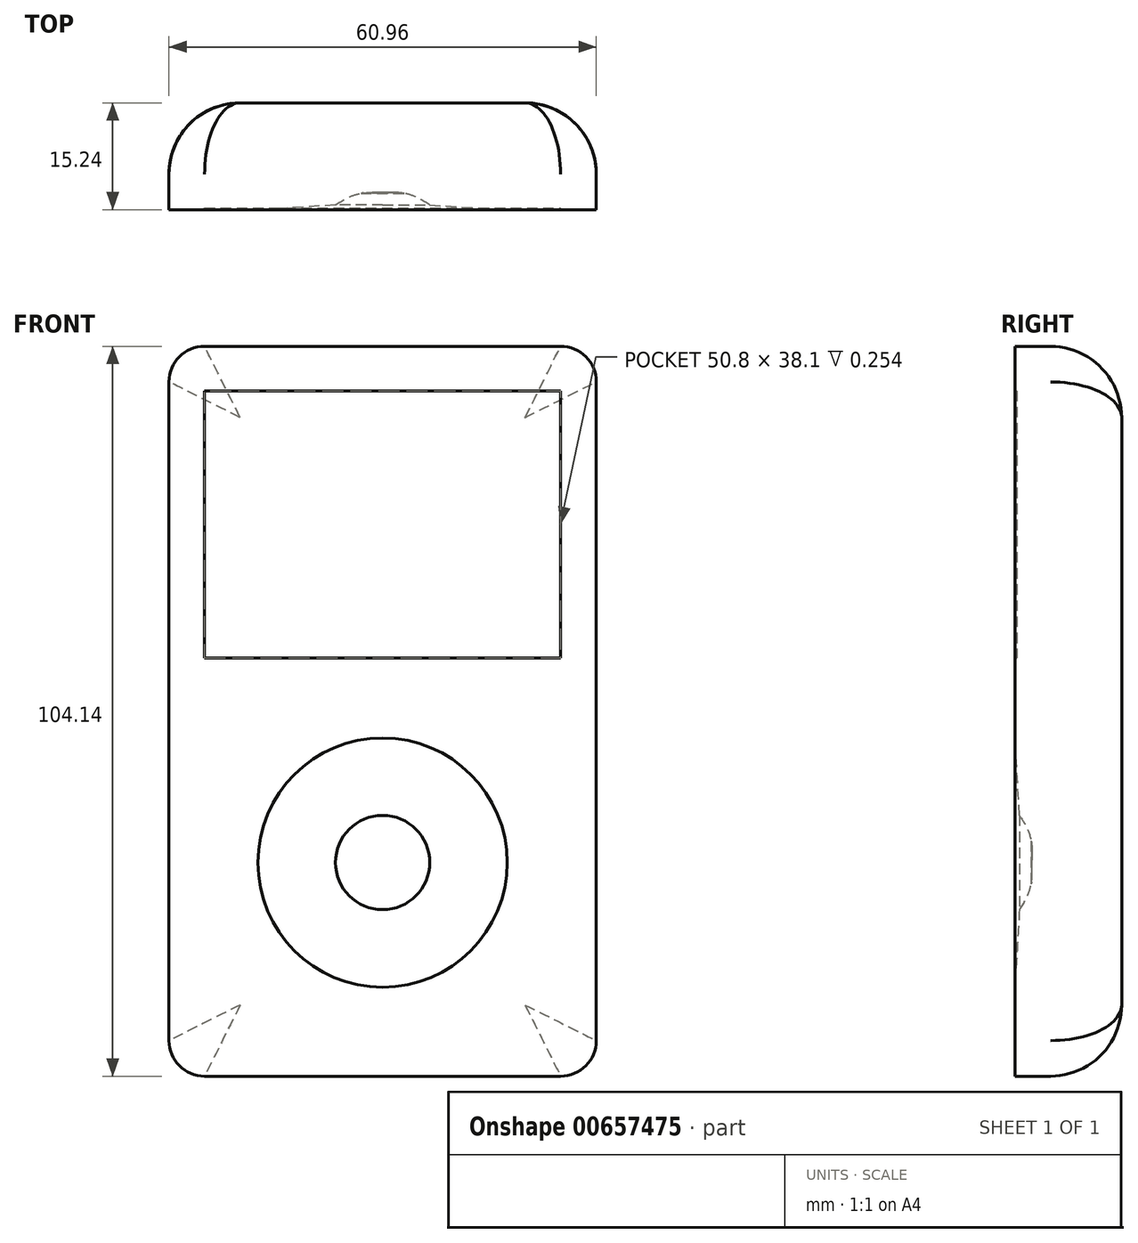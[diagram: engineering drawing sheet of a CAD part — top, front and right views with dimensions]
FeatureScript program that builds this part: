
annotation { "Feature Type Name" : "Feature", "Feature Type Description" : "" }
export const myFeature = defineFeature(function(context is Context, id is Id, definition is map)
    precondition{}
    {
        {
            var Q0;
            Q0=qCreatedBy(makeId("Front.planeOp"),FACE);
            var sketch = newSketch(context, id + "F0", { "sketchPlane" : qUnion([Q0])});
            skLineSegment(sketch, "E0", {"start": v(0, 73.66) * mm, "end": v(0, -58.61) * mm, "construction": true});
            skCircle(sketch, "E1", {"center": v(0, 0) * mm, "radius": 17.78 * mm});
            skCircle(sketch, "E2", {"center": v(0, 0) * mm, "radius": 7.62 * mm});
            skLineSegment(sketch, "E3", {"start": v(0, 73.66) * mm, "end": v(25.4, 73.66) * mm});
            skLineSegment(sketch, "E4", {"start": v(30.48, 68.58) * mm, "end": v(30.48, -25.4) * mm});
            skLineSegment(sketch, "E5", {"start": v(25.4, -30.48) * mm, "end": v(0, -30.48) * mm});
            skLineSegment(sketch, "E6", {"start": v(0, 67.31) * mm, "end": v(25.4, 67.31) * mm});
            skLineSegment(sketch, "E7", {"start": v(25.4, 67.31) * mm, "end": v(25.4, 29.21) * mm});
            skLineSegment(sketch, "E8", {"start": v(25.4, 29.21) * mm, "end": v(0, 29.21) * mm});
            skPoint(sketch, "E9", {"position": v(25.4, 48.26) * mm});
            skLineSegment(sketch, "E10.MirrorCS", {"start": v(-25.4, 29.21) * mm, "end": v(0, 29.21) * mm});
            skLineSegment(sketch, "E11.MirrorCS", {"start": v(-25.4, 67.31) * mm, "end": v(-25.4, 29.21) * mm});
            skLineSegment(sketch, "E12.MirrorCS", {"start": v(0, 67.31) * mm, "end": v(-25.4, 67.31) * mm});
            skLineSegment(sketch, "E13.MirrorCS", {"start": v(0, 73.66) * mm, "end": v(-25.4, 73.66) * mm});
            skLineSegment(sketch, "E14.MirrorCS", {"start": v(-30.48, 68.58) * mm, "end": v(-30.48, -25.4) * mm});
            skLineSegment(sketch, "E15.MirrorCS", {"start": v(-25.4, -30.48) * mm, "end": v(0, -30.48) * mm});
            skPoint(sketch, "E16.visualSharp", {"position": v(-30.48, 73.66) * mm});
            skArc(sketch, "E16.filletArc", {"start": v(-25.4, 73.66) * mm, "mid": v(-29, 72.17) * mm, "end": v(-30.48, 68.58) * mm});
            skPoint(sketch, "E17.visualSharp", {"position": v(30.48, 73.66) * mm});
            skArc(sketch, "E17.filletArc", {"start": v(30.48, 68.58) * mm, "mid": v(29, 72.17) * mm, "end": v(25.4, 73.66) * mm});
            skPoint(sketch, "E18.visualSharp", {"position": v(30.48, -30.48) * mm});
            skArc(sketch, "E18.filletArc", {"start": v(25.4, -30.48) * mm, "mid": v(29, -29) * mm, "end": v(30.48, -25.4) * mm});
            skPoint(sketch, "E19.visualSharp", {"position": v(-30.48, -30.48) * mm});
            skArc(sketch, "E19.filletArc", {"start": v(-30.48, -25.4) * mm, "mid": v(-29, -29) * mm, "end": v(-25.4, -30.48) * mm});
            skSolve(sketch);
        }
        {
            var Q0;
            Q0 = qSketchRegion(id + "F0", true);
            extrude(context, id + "F1", {"entities" : qUnion([Q0]), "depth" : 15.24 * mm, "offsetDistance" : 25 * mm});
        }
        {
            var Q0;
            Q0=makeQuery(id+"F0.imprint","IMPRINT",FACE,{"disambiguationData":[TD([[makeQuery(id+"F0.imprint","IMPRINT",EDGE,{"derivedFrom":sQuery(id+"F0.wireOp",EDGE,"E6")}),-1.0]])]});
            extrude(context, id + "F2", {"entities" : qUnion([Q0]), "operationType" : NewBodyOperationType.ADD, "depth" : 15 * mm, "offsetDistance" : 25 * mm});
        }
        {
            var Q0;
            Q0=qCreatedBy(makeId("Right.planeOp"),FACE);
            var sketch = newSketch(context, id + "F3", { "sketchPlane" : qUnion([Q0])});
            skLineSegment(sketch, "E20.0", {"start": v(0, -17.78) * mm, "end": v(0, 17.78) * mm});
            skLineSegment(sketch, "E21.top", {"start": v(0, -17.78) * mm, "end": v(-15.24, -17.78) * mm});
            skLineSegment(sketch, "E21.left", {"start": v(0, 0) * mm, "end": v(0, -17.78) * mm});
            skLineSegment(sketch, "E22", {"start": v(-12.93, -3.1) * mm, "end": v(-12.87, -2.76) * mm});
            skPoint(sketch, "E23", {"position": v(-15.24, -7.62) * mm});
            skFitSpline(sketch, "E24", {"points": [v(-15.24, -7.62) * mm, v(-12.93, -3.1) * mm, v(-13.93, 5.74) * mm], "startDerivative": vector(6.9, 9.44) * mm, "endDerivative": vector(-3.8, 16.93) * mm});
            skPoint(sketch, "E25.orphan", {"position": v(-15.24, 0) * mm});
            skLineSegment(sketch, "E26", {"start": v(0, 0) * mm, "end": v(-12.87, 0) * mm});
            skLineSegment(sketch, "E27", {"start": v(-15.24, -17.78) * mm, "end": v(-14.6, -6.72) * mm});
            skSolve(sketch);
        }
        {
            var Q0;
            Q0=makeQuery(id+"F3.imprint","IMPRINT",FACE,{"disambiguationData":[TD([[makeQuery(id+"F3.imprint","IMPRINT",EDGE,{"derivedFrom":sQuery(id+"F3.wireOp",EDGE,"E21.top")}),-1.0]])]});
            var Q1;
            Q1=sQuery(id+"F3.wireOp",EDGE,"E26");
            revolve(context, id + "F4", {"operationType" : NewBodyOperationType.ADD, "entities" : qUnion([Q0]), "axis" : qUnion([Q1]), "revolveType" : RevolveType.FULL});
        }
        {
            var Q0;
            Q0=makeQuery(id+"F1.opExtrude","CAP_EDGE",EDGE,{"disambiguationData":[OSD([sQuery(id+"F0.wireOp",EDGE,"E4")])],"isStart":true});
            fillet(context, id + "F5", {"entities" : qUnion([Q0]), "radius" : 10.16 * mm, "tangentPropagation" : true, "allowEdgeOverflow" : false});
        }
    });
